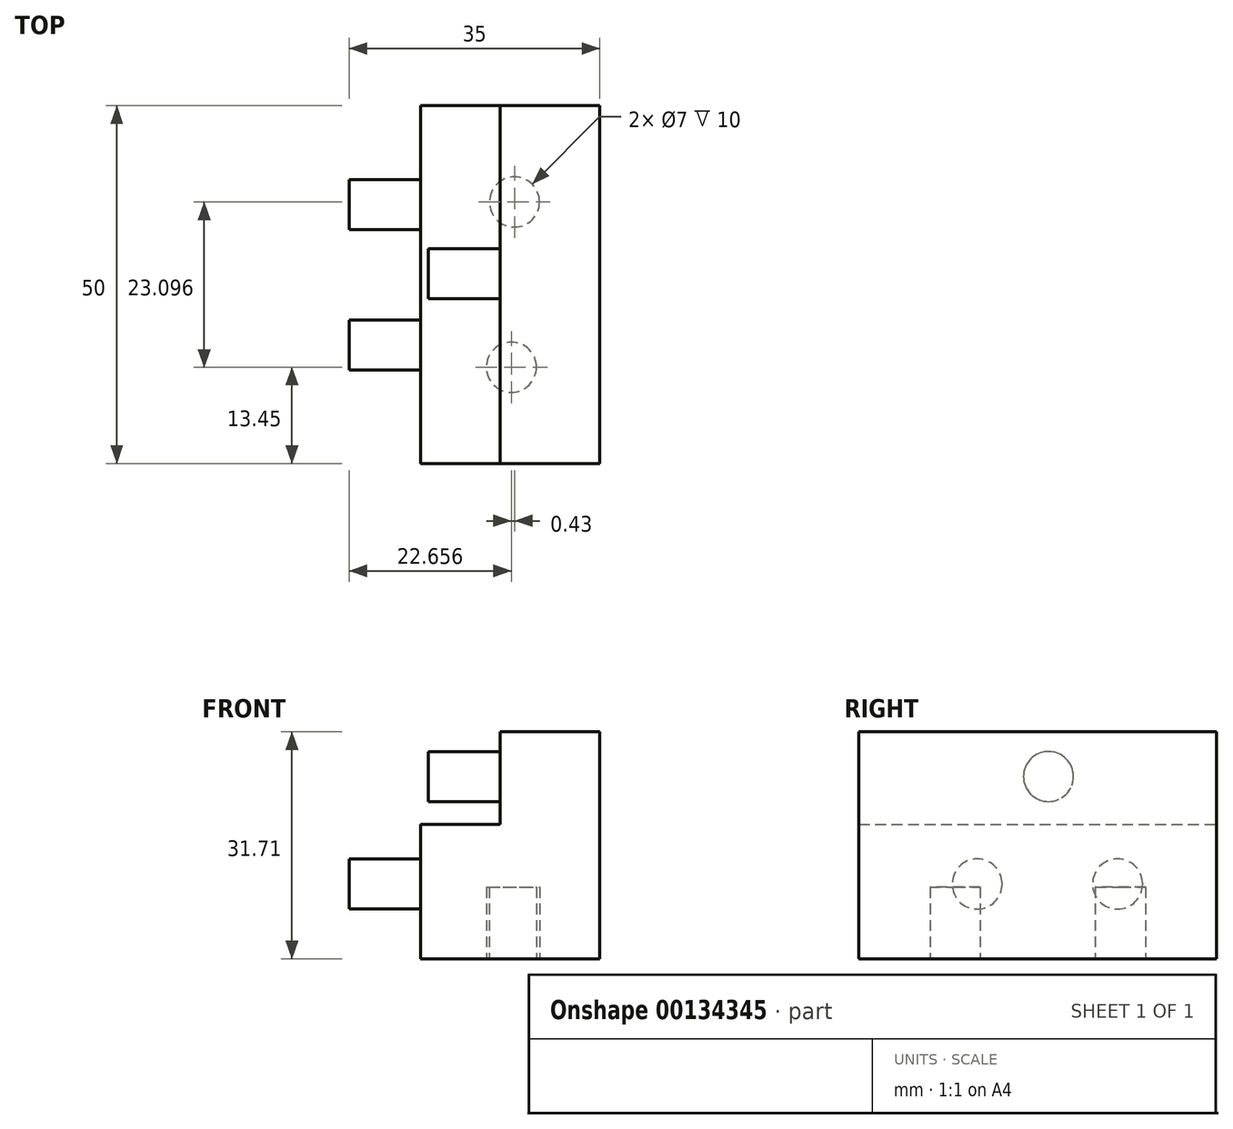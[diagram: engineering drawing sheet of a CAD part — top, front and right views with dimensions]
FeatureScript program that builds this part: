
annotation { "Feature Type Name" : "Feature", "Feature Type Description" : "" }
export const myFeature = defineFeature(function(context is Context, id is Id, definition is map)
    precondition{}
    {
        {
            var Q0;
            Q0=qCreatedBy(makeId("Front.planeOp"),FACE);
            var sketch = newSketch(context, id + "F0", { "sketchPlane" : qUnion([Q0])});
            skLineSegment(sketch, "E0.bottom", {"start": v(25, -25) * mm, "end": v(-25, -25) * mm});
            skLineSegment(sketch, "E0.top", {"start": v(25, 25) * mm, "end": v(-25, 25) * mm});
            skLineSegment(sketch, "E0.left", {"start": v(25, -25) * mm, "end": v(25, 25) * mm});
            skLineSegment(sketch, "E0.right", {"start": v(-25, -25) * mm, "end": v(-25, 25) * mm});
            skPoint(sketch, "E0.middle", {"position": v(0, 0) * mm});
            skLineSegment(sketch, "E1", {"start": v(11.08, 25) * mm, "end": v(11.08, 12.09) * mm});
            skLineSegment(sketch, "E2", {"start": v(11.08, 12.09) * mm, "end": v(-11.2, 12.09) * mm});
            skLineSegment(sketch, "E3", {"start": v(-11.2, 12.09) * mm, "end": v(-11.2, 25) * mm});
            skLineSegment(sketch, "E4", {"start": v(25, -6.71) * mm, "end": v(0, -6.71) * mm});
            skLineSegment(sketch, "E5", {"start": v(0, -6.71) * mm, "end": v(0, 12.09) * mm});
            skLineSegment(sketch, "E6", {"start": v(0, -6.71) * mm, "end": v(-25, -25) * mm});
            skSolve(sketch);
        }
        {
            var Q0;
            {var subQ1=sQuery(id+"F0.wireOp",EDGE,"E1");Q0=makeQuery(id+"F0.imprint","IMPRINT",FACE,{"disambiguationData":[TD([[makeQuery(id+"F0.imprint","IMPRINT",EDGE,{"derivedFrom":subQ1}),1.0]])]});}
            extrude(context, id + "F1", {"entities" : qUnion([Q0]), "depth" : 50 * mm});
        }
        {
            var Q0;
            Q0=makeQuery(id+"F1.opExtrude","SWEPT_FACE",FACE,{"disambiguationData":[OSD([sQuery(id+"F0.wireOp",EDGE,"E5")])]});
            var sketch = newSketch(context, id + "F2", { "sketchPlane" : qUnion([Q0])});
            skCircle(sketch, "E7", {"center": v(13.84, 3.73) * mm, "radius": 3.5 * mm});
            skCircle(sketch, "E8", {"center": v(33.46, 3.73) * mm, "radius": 3.5 * mm});
            skSolve(sketch);
        }
        {
            var Q0;
            Q0=makeQuery(id+"F2.imprint","IMPRINT",FACE,{"disambiguationData":[TD([[makeQuery(id+"F2.imprint","IMPRINT",EDGE,{"derivedFrom":sQuery(id+"F2.wireOp",EDGE,"E7")}),1.0]])]});
            var Q1;
            Q1=makeQuery(id+"F2.imprint","IMPRINT",FACE,{"disambiguationData":[TD([[makeQuery(id+"F2.imprint","IMPRINT",EDGE,{"derivedFrom":sQuery(id+"F2.wireOp",EDGE,"E8")}),1.0]])]});
            var Q2;
            Q2=makeQuery(id+"F2.imprint","IMPRINT",FACE,{"disambiguationData":[TD([[makeQuery(id+"F2.imprint","IMPRINT",EDGE,{"derivedFrom":sQuery(id+"F2.wireOp",EDGE,"Be7NQzTP-gcJt-BU9h-l8M0-Qa6RHLMFE50P")}),1.0]])]});
            extrude(context, id + "F3", {"entities" : qUnion([Q0, Q1, Q2]), "operationType" : NewBodyOperationType.ADD, "depth" : 10 * mm});
        }
        {
            var Q0;
            Q0=makeQuery(id+"F1.opExtrude","SWEPT_FACE",FACE,{"disambiguationData":[OSD([sQuery(id+"F0.wireOp",EDGE,"E4")])]});
            var sketch = newSketch(context, id + "F4", { "sketchPlane" : qUnion([Q0])});
            skCircle(sketch, "E9", {"center": v(13.09, 13.45) * mm, "radius": 3.5 * mm});
            skCircle(sketch, "E10", {"center": v(12.66, 36.55) * mm, "radius": 3.5 * mm});
            skSolve(sketch);
        }
        {
            var Q0;
            Q0=makeQuery(id+"F4.imprint","IMPRINT",FACE,{"disambiguationData":[TD([[makeQuery(id+"F4.imprint","IMPRINT",EDGE,{"derivedFrom":sQuery(id+"F4.wireOp",EDGE,"E10")}),1.0]])]});
            var Q1;
            Q1=makeQuery(id+"F4.imprint","IMPRINT",FACE,{"disambiguationData":[TD([[makeQuery(id+"F4.imprint","IMPRINT",EDGE,{"derivedFrom":sQuery(id+"F4.wireOp",EDGE,"E9")}),1.0]])]});
            extrude(context, id + "F5", {"entities" : qUnion([Q0, Q1]), "operationType" : NewBodyOperationType.REMOVE, "oppositeDirection" : true, "depth" : 10 * mm});
        }
        {
            var Q0;
            Q0=makeQuery(id+"F1.opExtrude","SWEPT_FACE",FACE,{"disambiguationData":[OSD([sQuery(id+"F0.wireOp",EDGE,"E1")])]});
            var sketch = newSketch(context, id + "F6", { "sketchPlane" : qUnion([Q0])});
            skCircle(sketch, "E11", {"center": v(23.5, 18.75) * mm, "radius": 3.5 * mm});
            skSolve(sketch);
        }
        {
            var Q0;
            Q0=makeQuery(id+"F6.imprint","IMPRINT",FACE,{"disambiguationData":[TD([[makeQuery(id+"F6.imprint","IMPRINT",EDGE,{"derivedFrom":sQuery(id+"F6.wireOp",EDGE,"E11")}),1.0]])]});
            extrude(context, id + "F7", {"entities" : qUnion([Q0]), "operationType" : NewBodyOperationType.ADD, "depth" : 10 * mm});
        }
    });
